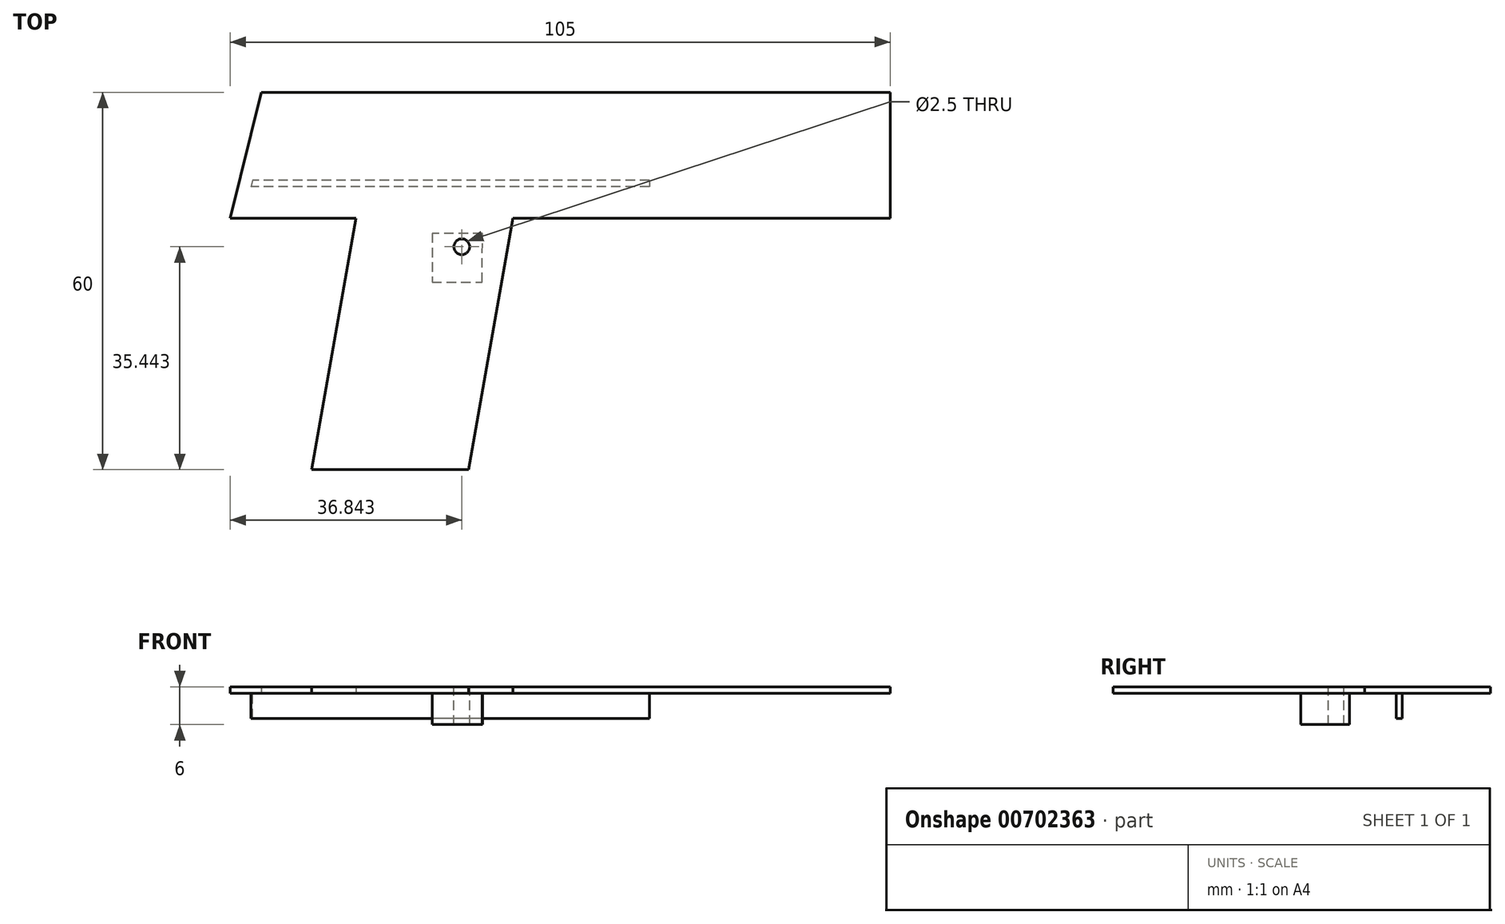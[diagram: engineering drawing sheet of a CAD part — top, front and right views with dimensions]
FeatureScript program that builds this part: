
annotation { "Feature Type Name" : "Feature", "Feature Type Description" : "" }
export const myFeature = defineFeature(function(context is Context, id is Id, definition is map)
    precondition{}
    {
        {
            var Q0;
            Q0=qCreatedBy(makeId("Top.planeOp"),FACE);
            var sketch = newSketch(context, id + "F0", { "sketchPlane" : qUnion([Q0])});
            skLineSegment(sketch, "E0", {"start": v(-39.8, 26.27) * mm, "end": v(60.2, 26.27) * mm});
            skLineSegment(sketch, "E1", {"start": v(60.2, 26.27) * mm, "end": v(60.2, 6.27) * mm});
            skLineSegment(sketch, "E2", {"start": v(60.2, 6.27) * mm, "end": v(0.2, 6.27) * mm});
            skLineSegment(sketch, "E3", {"start": v(0.2, 6.27) * mm, "end": v(-6.86, -33.73) * mm});
            skLineSegment(sketch, "E4", {"start": v(-6.86, -33.73) * mm, "end": v(-31.86, -33.73) * mm});
            skLineSegment(sketch, "E5", {"start": v(-31.86, -33.73) * mm, "end": v(-24.8, 6.27) * mm});
            skLineSegment(sketch, "E6", {"start": v(-24.8, 6.27) * mm, "end": v(-44.8, 6.27) * mm});
            skLineSegment(sketch, "E7", {"start": v(-44.8, 6.27) * mm, "end": v(-39.8, 26.27) * mm});
            skSolve(sketch);
        }
        {
            var Q0;
            Q0=makeQuery(id+"F0.imprint","IMPRINT",FACE,{"disambiguationData":[TD([[makeQuery(id+"F0.imprint","IMPRINT",EDGE,{"derivedFrom":sQuery(id+"F0.wireOp",EDGE,"E0")}),-1.0]])]});
            extrude(context, id + "F1", {"entities" : qUnion([Q0]), "endBound" : BoundingType.SYMMETRIC, "depth" : 19 * mm, "offsetDistance" : 25 * mm});
        }
        {
            var Q0;
            Q0=makeQuery(id+"F1.opExtrude","CAP_FACE",FACE,{"disambiguationData":[OSD([sQuery(id+"F0.wireOp",EDGE,"E0"),sQuery(id+"F0.wireOp",EDGE,"E1"),sQuery(id+"F0.wireOp",EDGE,"E2"),sQuery(id+"F0.wireOp",EDGE,"E3"),sQuery(id+"F0.wireOp",EDGE,"E4"),sQuery(id+"F0.wireOp",EDGE,"E5"),sQuery(id+"F0.wireOp",EDGE,"E6"),sQuery(id+"F0.wireOp",EDGE,"E7")])],"isStart":false});
            var sketch = newSketch(context, id + "F2", { "sketchPlane" : qUnion([Q0])});
            skLineSegment(sketch, "E8", {"start": v(-38.12, 24.77) * mm, "end": v(-42.24, 8.27) * mm});
            skLineSegment(sketch, "E9", {"start": v(-42.24, 8.27) * mm, "end": v(-22.42, 8.27) * mm});
            skLineSegment(sketch, "E10", {"start": v(-22.42, 8.27) * mm, "end": v(-27.3, -19.4) * mm});
            skLineSegment(sketch, "E11", {"start": v(-27.3, -19.4) * mm, "end": v(-6.36, -19.4) * mm});
            skLineSegment(sketch, "E12", {"start": v(-6.36, -19.4) * mm, "end": v(-1.83, 6.27) * mm});
            skLineSegment(sketch, "E13", {"start": v(-1.83, 6.27) * mm, "end": v(-17.42, 6.27) * mm});
            skLineSegment(sketch, "E14", {"start": v(-17.42, 6.27) * mm, "end": v(-17.42, 8.27) * mm});
            skLineSegment(sketch, "E15", {"start": v(-17.42, 8.27) * mm, "end": v(56.88, 8.27) * mm});
            skLineSegment(sketch, "E16", {"start": v(56.88, 8.27) * mm, "end": v(56.88, 11.27) * mm});
            skLineSegment(sketch, "E17", {"start": v(-38.12, 24.77) * mm, "end": v(21.88, 24.77) * mm});
            skLineSegment(sketch, "E18", {"start": v(21.88, 24.77) * mm, "end": v(21.88, 11.27) * mm});
            skLineSegment(sketch, "E19", {"start": v(21.88, 11.27) * mm, "end": v(56.88, 11.27) * mm});
            skSolve(sketch);
        }
        {
            var Q0;
            Q0=makeQuery(id+"F2.imprint","IMPRINT",FACE,{"disambiguationData":[TD([[makeQuery(id+"F2.imprint","IMPRINT",EDGE,{"derivedFrom":sQuery(id+"F2.wireOp",EDGE,"E8")}),1.0]])]});
            extrude(context, id + "F3", {"entities" : qUnion([Q0]), "operationType" : NewBodyOperationType.REMOVE, "oppositeDirection" : true, "depth" : 18 * mm, "offsetDistance" : 25 * mm});
        }
        {
            var Q0;
            Q0=makeQuery(id+"F1.opExtrude","SWEPT_FACE",FACE,{"disambiguationData":[OSD([sQuery(id+"F0.wireOp",EDGE,"E1")])]});
            var sketch = newSketch(context, id + "F4", { "sketchPlane" : qUnion([Q0])});
            skLineSegment(sketch, "E20", {"start": v(26.27, 9.5) * mm, "end": v(6.27, -9.5) * mm, "construction": true});
            skLineSegment(sketch, "E21", {"start": v(26.27, -9.5) * mm, "end": v(6.27, 9.5) * mm, "construction": true});
            skLineSegment(sketch, "E22", {"start": v(16.27, 0) * mm, "end": v(19.77, 0) * mm, "construction": true});
            skCircle(sketch, "E23", {"center": v(19.77, 0) * mm, "radius": 4.5 * mm});
            skSolve(sketch);
        }
        {
            var Q0;
            Q0=makeQuery(id+"F4.imprint","IMPRINT",FACE,{"disambiguationData":[TD([[makeQuery(id+"F4.imprint","IMPRINT",EDGE,{"derivedFrom":sQuery(id+"F4.wireOp",EDGE,"E23")}),1.0]])]});
            extrude(context, id + "F5", {"entities" : qUnion([Q0]), "operationType" : NewBodyOperationType.REMOVE, "oppositeDirection" : true, "depth" : 40 * mm, "offsetDistance" : 25 * mm});
        }
        {
            var Q0;
            Q0=qCreatedBy(makeId("Top.planeOp"),FACE);
            var sketch = newSketch(context, id + "F6", { "sketchPlane" : qUnion([Q0])});
            skLineSegment(sketch, "E24", {"start": v(21.8, 29.03) * mm, "end": v(21.8, 22.05) * mm});
            skLineSegment(sketch, "E25", {"start": v(21.8, 22.05) * mm, "end": v(-29.62, 22.05) * mm});
            skLineSegment(sketch, "E26", {"start": v(-29.62, 22.05) * mm, "end": v(-29.62, 28.4) * mm});
            skLineSegment(sketch, "E27", {"start": v(-29.62, 28.4) * mm, "end": v(21.8, 29.03) * mm});
            skSolve(sketch);
        }
        {
            var Q0;
            Q0=makeQuery(id+"F6.imprint","IMPRINT",FACE,{"disambiguationData":[TD([[makeQuery(id+"F6.imprint","IMPRINT",EDGE,{"derivedFrom":sQuery(id+"F6.wireOp",EDGE,"E24")}),-1.0]])]});
            extrude(context, id + "F7", {"entities" : qUnion([Q0]), "operationType" : NewBodyOperationType.REMOVE, "endBound" : BoundingType.SYMMETRIC, "oppositeDirection" : true, "depth" : 2 * mm, "offsetDistance" : 25 * mm});
        }
        {
            var Q0;
            Q0=makeQuery(id+"F3.boolean.opBoolean","COPY",FACE,{"derivedFrom":makeQuery(id+"F3.opExtrude","CAP_FACE",FACE,{"disambiguationData":[OSD([sQuery(id+"F2.wireOp",EDGE,"E8"),sQuery(id+"F2.wireOp",EDGE,"E9"),sQuery(id+"F2.wireOp",EDGE,"E10"),sQuery(id+"F2.wireOp",EDGE,"E11"),sQuery(id+"F2.wireOp",EDGE,"E12"),sQuery(id+"F2.wireOp",EDGE,"E13"),sQuery(id+"F2.wireOp",EDGE,"E14"),sQuery(id+"F2.wireOp",EDGE,"E15"),sQuery(id+"F2.wireOp",EDGE,"E16"),sQuery(id+"F2.wireOp",EDGE,"E17"),sQuery(id+"F2.wireOp",EDGE,"E18"),sQuery(id+"F2.wireOp",EDGE,"E19")])],"isStart":false})});
            var sketch = newSketch(context, id + "F8", { "sketchPlane" : qUnion([Q0])});
            skLineSegment(sketch, "E28", {"start": v(21.88, 11.27) * mm, "end": v(-41.5, 11.27) * mm});
            skLineSegment(sketch, "E29", {"start": v(21.88, 11.27) * mm, "end": v(21.88, 12.27) * mm});
            skLineSegment(sketch, "E30", {"start": v(21.88, 12.27) * mm, "end": v(-41.24, 12.27) * mm});
            skLineSegment(sketch, "E31", {"start": v(-41.24, 12.27) * mm, "end": v(-41.5, 11.27) * mm});
            skLineSegment(sketch, "E32", {"start": v(21.88, 24.77) * mm, "end": v(21.88, 21.77) * mm});
            skLineSegment(sketch, "E33", {"start": v(21.88, 24.77) * mm, "end": v(20.88, 24.77) * mm});
            skLineSegment(sketch, "E34", {"start": v(20.88, 24.77) * mm, "end": v(20.88, 21.77) * mm});
            skLineSegment(sketch, "E35", {"start": v(20.88, 21.77) * mm, "end": v(21.88, 21.77) * mm});
            skLineSegment(sketch, "E36", {"start": v(21.88, 12.27) * mm, "end": v(21.88, 15.27) * mm});
            skLineSegment(sketch, "E37", {"start": v(21.88, 15.27) * mm, "end": v(20.88, 15.27) * mm});
            skLineSegment(sketch, "E38", {"start": v(20.88, 15.27) * mm, "end": v(20.88, 12.27) * mm});
            skLineSegment(sketch, "E39", {"start": v(20.88, 12.27) * mm, "end": v(21.88, 12.27) * mm});
            skSolve(sketch);
        }
        {
            var Q0;
            Q0=makeQuery(id+"F8.imprint","IMPRINT",FACE,{"disambiguationData":[TD([[makeQuery(id+"F8.imprint","IMPRINT",EDGE,{"derivedFrom":sQuery(id+"F8.wireOp",EDGE,"E28")}),-1.0]])]});
            extrude(context, id + "F9", {"entities" : qUnion([Q0]), "operationType" : NewBodyOperationType.ADD, "depth" : 5 * mm, "offsetDistance" : 25 * mm});
        }
        {
            var Q0;
            Q0=makeQuery(id+"F8.imprint","IMPRINT",FACE,{"disambiguationData":[TD([[makeQuery(id+"F8.imprint","IMPRINT",EDGE,{"derivedFrom":sQuery(id+"F8.wireOp",EDGE,"E32")}),-1.0]])]});
            var Q1;
            Q1=makeQuery(id+"F1.opExtrude","CAP_FACE",FACE,{"disambiguationData":[OSD([sQuery(id+"F0.wireOp",EDGE,"E0"),sQuery(id+"F0.wireOp",EDGE,"E1"),sQuery(id+"F0.wireOp",EDGE,"E2"),sQuery(id+"F0.wireOp",EDGE,"E3"),sQuery(id+"F0.wireOp",EDGE,"E4"),sQuery(id+"F0.wireOp",EDGE,"E5"),sQuery(id+"F0.wireOp",EDGE,"E6"),sQuery(id+"F0.wireOp",EDGE,"E7")])],"isStart":false});
            extrude(context, id + "F10", {"entities" : qUnion([Q0]), "operationType" : NewBodyOperationType.ADD, "endBound" : BoundingType.UP_TO_SURFACE, "depth" : 18 * mm, "endBoundEntityFace" : qUnion([Q1]), "offsetDistance" : 25 * mm});
        }
        {
            var Q0;
            Q0=makeQuery(id+"F8.imprint","IMPRINT",FACE,{"disambiguationData":[TD([[makeQuery(id+"F8.imprint","IMPRINT",EDGE,{"derivedFrom":sQuery(id+"F8.wireOp",EDGE,"E36")}),-1.0]])]});
            var Q1;
            {var subQ0=sQuery(id+"F0.wireOp",EDGE,"E7");var subQ1=sQuery(id+"F0.wireOp",EDGE,"E6");var subQ2=sQuery(id+"F0.wireOp",EDGE,"E5");var subQ3=sQuery(id+"F0.wireOp",EDGE,"E4");var subQ4=sQuery(id+"F0.wireOp",EDGE,"E3");var subQ5=sQuery(id+"F0.wireOp",EDGE,"E2");var subQ6=sQuery(id+"F0.wireOp",EDGE,"E1");var subQ7=sQuery(id+"F0.wireOp",EDGE,"E0");Q1=makeQuery(id+"F10.boolean.opBoolean","MERGE",FACE,{"derivedFrom":[makeQuery(id+"F1.opExtrude","CAP_FACE",FACE,{"disambiguationData":[OSD([subQ7,subQ6,subQ5,subQ4,subQ3,subQ2,subQ1,subQ0])],"isStart":false}),makeQuery(id+"F10.opExtrude","CAP_FACE",FACE,{"disambiguationData":[OSD([subQ7,subQ6,subQ5,subQ4,subQ3,subQ2,subQ1,subQ0])],"isStart":false})]});}
            extrude(context, id + "F11", {"entities" : qUnion([Q0]), "operationType" : NewBodyOperationType.ADD, "endBound" : BoundingType.UP_TO_SURFACE, "depth" : 25 * mm, "endBoundEntityFace" : qUnion([Q1]), "offsetDistance" : 25 * mm});
        }
        {
            var Q0;
            Q0=makeQuery(id+"F1.opExtrude","SWEPT_FACE",FACE,{"disambiguationData":[OSD([sQuery(id+"F0.wireOp",EDGE,"E2")])]});
            var sketch = newSketch(context, id + "F12", { "sketchPlane" : qUnion([Q0])});
            skLineSegment(sketch, "E40", {"start": v(60.2, 0) * mm, "end": v(52.2, 0) * mm, "construction": true});
            skCircle(sketch, "E41", {"center": v(52.2, 0) * mm, "radius": 1 * mm});
            skSolve(sketch);
        }
        {
            var Q0;
            Q0=makeQuery(id+"F12.imprint","IMPRINT",FACE,{"disambiguationData":[TD([[makeQuery(id+"F12.imprint","IMPRINT",EDGE,{"derivedFrom":sQuery(id+"F12.wireOp",EDGE,"E41")}),1.0]])]});
            extrude(context, id + "F13", {"entities" : qUnion([Q0]), "operationType" : NewBodyOperationType.REMOVE, "oppositeDirection" : true, "depth" : 6.9 * mm, "offsetDistance" : 25 * mm});
        }
        {
            var Q0;
            Q0=qCreatedBy(makeId("Top.planeOp"),FACE);
            var sketch = newSketch(context, id + "F14", { "sketchPlane" : qUnion([Q0])});
            skLineSegment(sketch, "E42", {"start": v(-9.72, 1.27) * mm, "end": v(7.04, 1.27) * mm});
            skLineSegment(sketch, "E43", {"start": v(7.04, 1.27) * mm, "end": v(7.04, -10.73) * mm});
            skLineSegment(sketch, "E44", {"start": v(7.04, -10.73) * mm, "end": v(-8.95, -10.73) * mm});
            skLineSegment(sketch, "E45", {"start": v(-8.95, -10.73) * mm, "end": v(-9.72, 1.27) * mm});
            skSolve(sketch);
        }
        {
            var Q0;
            Q0=makeQuery(id+"F14.imprint","IMPRINT",FACE,{"disambiguationData":[TD([[makeQuery(id+"F14.imprint","IMPRINT",EDGE,{"derivedFrom":sQuery(id+"F14.wireOp",EDGE,"E42")}),-1.0]])]});
            extrude(context, id + "F15", {"entities" : qUnion([Q0]), "operationType" : NewBodyOperationType.REMOVE, "endBound" : BoundingType.SYMMETRIC, "oppositeDirection" : true, "depth" : 6 * mm, "offsetDistance" : 25 * mm});
        }
        {
            var Q0;
            {var subQ0=sQuery(id+"F2.wireOp",EDGE,"E19");var subQ1=sQuery(id+"F2.wireOp",EDGE,"E16");var subQ2=sQuery(id+"F2.wireOp",EDGE,"E15");var subQ3=sQuery(id+"F2.wireOp",EDGE,"E14");var subQ4=sQuery(id+"F2.wireOp",EDGE,"E13");var subQ5=sQuery(id+"F2.wireOp",EDGE,"E12");var subQ6=sQuery(id+"F2.wireOp",EDGE,"E8");var subQ7=sQuery(id+"F2.wireOp",EDGE,"E9");var subQ8=sQuery(id+"F2.wireOp",EDGE,"E10");var subQ9=sQuery(id+"F2.wireOp",EDGE,"E11");Q0=makeQuery(id+"F9.boolean.opBoolean","SPLIT",FACE,{"disambiguationData":[TD([makeQuery(id+"F3.boolean.opBoolean","COPY",FACE,{"derivedFrom":makeQuery(id+"F3.opExtrude","SWEPT_FACE",FACE,{"disambiguationData":[OSD([subQ7])]})})])],"derivedFrom":makeQuery(id+"F3.boolean.opBoolean","COPY",FACE,{"derivedFrom":makeQuery(id+"F3.opExtrude","CAP_FACE",FACE,{"disambiguationData":[OSD([subQ6,subQ7,subQ8,subQ9,subQ5,subQ4,subQ3,subQ2,subQ1,sQuery(id+"F2.wireOp",EDGE,"E17"),sQuery(id+"F2.wireOp",EDGE,"E18"),subQ0])],"isStart":false})})});}
            var sketch = newSketch(context, id + "F16", { "sketchPlane" : qUnion([Q0])});
            skCircle(sketch, "E46", {"center": v(-7.96, 1.71) * mm, "radius": 1.25 * mm});
            skSolve(sketch);
        }
        {
            var Q0;
            Q0=makeQuery(id+"F16.imprint","IMPRINT",FACE,{"disambiguationData":[TD([[makeQuery(id+"F16.imprint","IMPRINT",EDGE,{"derivedFrom":sQuery(id+"F16.wireOp",EDGE,"E46")}),1.0]])]});
            extrude(context, id + "F17", {"entities" : qUnion([Q0]), "operationType" : NewBodyOperationType.REMOVE, "oppositeDirection" : true, "depth" : 5 * mm, "offsetDistance" : 25 * mm});
        }
        {
            var Q0;
            {var subQ0=sQuery(id+"F0.wireOp",EDGE,"E7");var subQ1=sQuery(id+"F0.wireOp",EDGE,"E6");var subQ2=sQuery(id+"F0.wireOp",EDGE,"E5");var subQ3=sQuery(id+"F0.wireOp",EDGE,"E4");var subQ4=sQuery(id+"F0.wireOp",EDGE,"E3");var subQ5=sQuery(id+"F0.wireOp",EDGE,"E2");var subQ6=sQuery(id+"F0.wireOp",EDGE,"E1");var subQ7=sQuery(id+"F0.wireOp",EDGE,"E0");Q0=makeQuery(id+"F11.boolean.opBoolean","MERGE",FACE,{"derivedFrom":[makeQuery(id+"F10.boolean.opBoolean","MERGE",FACE,{"derivedFrom":[makeQuery(id+"F1.opExtrude","CAP_FACE",FACE,{"disambiguationData":[OSD([subQ7,subQ6,subQ5,subQ4,subQ3,subQ2,subQ1,subQ0])],"isStart":false}),makeQuery(id+"F10.opExtrude","CAP_FACE",FACE,{"disambiguationData":[OSD([subQ7,subQ6,subQ5,subQ4,subQ3,subQ2,subQ1,subQ0])],"isStart":false})]}),makeQuery(id+"F11.opExtrude","CAP_FACE",FACE,{"disambiguationData":[OSD([subQ7,subQ6,subQ5,subQ4,subQ3,subQ2,subQ1,subQ0])],"isStart":false})]});}
            extrude(context, id + "F18", {"entities" : qUnion([Q0]), "operationType" : NewBodyOperationType.REMOVE, "oppositeDirection" : true, "depth" : 18 * mm, "offsetDistance" : 25 * mm});
        }
        {
            var Q0;
            Q0=makeQuery(id+"F9.opExtrude","CAP_FACE",FACE,{"disambiguationData":[OSD([sQuery(id+"F8.wireOp",EDGE,"E28"),sQuery(id+"F8.wireOp",EDGE,"E29"),sQuery(id+"F8.wireOp",EDGE,"E30"),sQuery(id+"F8.wireOp",EDGE,"E31"),sQuery(id+"F8.wireOp",EDGE,"E39")])],"isStart":false});
            extrude(context, id + "F19", {"entities" : qUnion([Q0]), "operationType" : NewBodyOperationType.ADD, "oppositeDirection" : true, "depth" : 10 * mm, "offsetDistance" : 25 * mm});
        }
        {
            var Q0;
            Q0=makeQuery(id+"F9.opExtrude","CAP_FACE",FACE,{"disambiguationData":[OSD([sQuery(id+"F8.wireOp",EDGE,"E28"),sQuery(id+"F8.wireOp",EDGE,"E29"),sQuery(id+"F8.wireOp",EDGE,"E30"),sQuery(id+"F8.wireOp",EDGE,"E31"),sQuery(id+"F8.wireOp",EDGE,"E39")])],"isStart":false});
            extrude(context, id + "F20", {"entities" : qUnion([Q0]), "operationType" : NewBodyOperationType.REMOVE, "oppositeDirection" : true, "depth" : 5 * mm, "offsetDistance" : 25 * mm});
        }
        {
            var Q0;
            Q0=makeQuery(id+"F1.opExtrude","CAP_FACE",FACE,{"disambiguationData":[OSD([sQuery(id+"F0.wireOp",EDGE,"E0"),sQuery(id+"F0.wireOp",EDGE,"E1"),sQuery(id+"F0.wireOp",EDGE,"E2"),sQuery(id+"F0.wireOp",EDGE,"E3"),sQuery(id+"F0.wireOp",EDGE,"E4"),sQuery(id+"F0.wireOp",EDGE,"E5"),sQuery(id+"F0.wireOp",EDGE,"E6"),sQuery(id+"F0.wireOp",EDGE,"E7")])],"isStart":true});
            var sketch = newSketch(context, id + "F21", { "sketchPlane" : qUnion([Q0])});
            skLineSegment(sketch, "E47", {"start": v(-4.67, -3.84) * mm, "end": v(-12.66, -3.84) * mm});
            skLineSegment(sketch, "E48", {"start": v(-12.66, -3.84) * mm, "end": v(-12.66, 3.89) * mm});
            skLineSegment(sketch, "E49", {"start": v(-12.66, 3.89) * mm, "end": v(-4.7, 3.89) * mm});
            skLineSegment(sketch, "E50", {"start": v(-4.7, 3.89) * mm, "end": v(-4.67, -3.84) * mm});
            skSolve(sketch);
        }
        {
            var Q0;
            Q0=makeQuery(id+"F21.imprint","IMPRINT",FACE,{"disambiguationData":[TD([[makeQuery(id+"F21.imprint","IMPRINT",EDGE,{"derivedFrom":sQuery(id+"F21.wireOp",EDGE,"E47")}),-1.0]])]});
            extrude(context, id + "F22", {"entities" : qUnion([Q0]), "operationType" : NewBodyOperationType.ADD, "depth" : 5 * mm, "offsetDistance" : 25 * mm});
        }
    });
